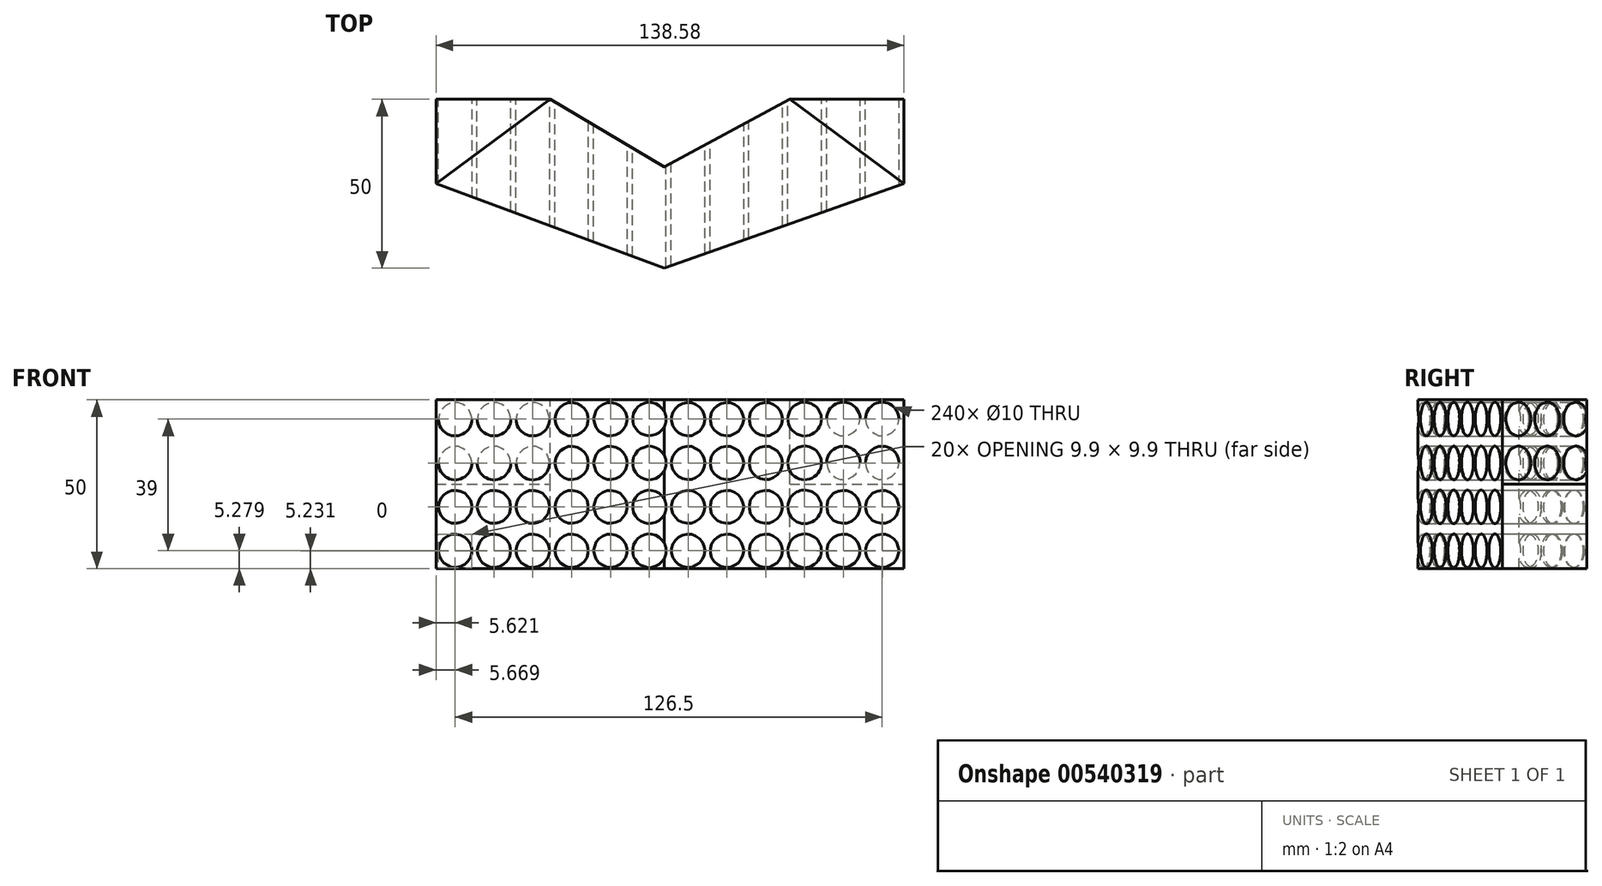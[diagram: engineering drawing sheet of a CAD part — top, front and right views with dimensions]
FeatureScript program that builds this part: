
annotation { "Feature Type Name" : "Feature", "Feature Type Description" : "" }
export const myFeature = defineFeature(function(context is Context, id is Id, definition is map)
    precondition{}
    {
        {
            var Q0;
            Q0=qCreatedBy(makeId("Front.planeOp"),FACE);
            var sketch = newSketch(context, id + "F0", { "sketchPlane" : qUnion([Q0])});
            skLineSegment(sketch, "E0.bottom", {"start": v(-67.58, 0) * mm, "end": v(71, 0) * mm});
            skLineSegment(sketch, "E0.top", {"start": v(-67.58, -50) * mm, "end": v(71, -50) * mm});
            skLineSegment(sketch, "E0.left", {"start": v(-67.58, 0) * mm, "end": v(-67.58, -50) * mm});
            skLineSegment(sketch, "E0.right", {"start": v(71, 0) * mm, "end": v(71, -50) * mm});
            skSolve(sketch);
        }
        {
            var Q0;
            Q0 = qSketchRegion(id + "F0", true);
            extrude(context, id + "F1", {"entities" : qUnion([Q0]), "depth" : 50 * mm, "offsetDistance" : 25 * mm});
        }
        {
            var Q0;
            Q0=makeQuery(id+"F0.imprint","IMPRINT",FACE,{"disambiguationData":[TD([[makeQuery(id+"F0.imprint","IMPRINT",EDGE,{"derivedFrom":sQuery(id+"F0.wireOp",EDGE,"E0.bottom")}),-1.0]])]});
            var sketch = newSketch(context, id + "F2", { "sketchPlane" : qUnion([Q0])});
            skCircle(sketch, "E1", {"center": v(-61.91, -5.72) * mm, "radius": 5 * mm});
            skCircle(sketch, "E2.0.1.0", {"center": v(-61.91, -18.72) * mm, "radius": 5 * mm});
            skCircle(sketch, "E2.0.2.0", {"center": v(-61.91, -31.72) * mm, "radius": 5 * mm});
            skCircle(sketch, "E2.0.3.0", {"center": v(-61.91, -44.72) * mm, "radius": 5 * mm});
            skCircle(sketch, "E2.1.0.0", {"center": v(-50.41, -5.72) * mm, "radius": 5 * mm});
            skCircle(sketch, "E2.1.1.0", {"center": v(-50.41, -18.72) * mm, "radius": 5 * mm});
            skCircle(sketch, "E2.1.2.0", {"center": v(-50.41, -31.72) * mm, "radius": 5 * mm});
            skCircle(sketch, "E2.1.3.0", {"center": v(-50.41, -44.72) * mm, "radius": 5 * mm});
            skCircle(sketch, "E2.2.0.0", {"center": v(-38.91, -5.72) * mm, "radius": 5 * mm});
            skCircle(sketch, "E2.2.1.0", {"center": v(-38.91, -18.72) * mm, "radius": 5 * mm});
            skCircle(sketch, "E2.2.2.0", {"center": v(-38.91, -31.72) * mm, "radius": 5 * mm});
            skCircle(sketch, "E2.2.3.0", {"center": v(-38.91, -44.72) * mm, "radius": 5 * mm});
            skCircle(sketch, "E2.3.0.0", {"center": v(-27.41, -5.72) * mm, "radius": 5 * mm});
            skCircle(sketch, "E2.3.1.0", {"center": v(-27.41, -18.72) * mm, "radius": 5 * mm});
            skCircle(sketch, "E2.3.2.0", {"center": v(-27.41, -31.72) * mm, "radius": 5 * mm});
            skCircle(sketch, "E2.3.3.0", {"center": v(-27.41, -44.72) * mm, "radius": 5 * mm});
            skCircle(sketch, "E2.4.0.0", {"center": v(-15.91, -5.72) * mm, "radius": 5 * mm});
            skCircle(sketch, "E2.4.1.0", {"center": v(-15.91, -18.72) * mm, "radius": 5 * mm});
            skCircle(sketch, "E2.4.2.0", {"center": v(-15.91, -31.72) * mm, "radius": 5 * mm});
            skCircle(sketch, "E2.4.3.0", {"center": v(-15.91, -44.72) * mm, "radius": 5 * mm});
            skCircle(sketch, "E2.5.0.0", {"center": v(-4.41, -5.72) * mm, "radius": 5 * mm});
            skCircle(sketch, "E2.5.1.0", {"center": v(-4.41, -18.72) * mm, "radius": 5 * mm});
            skCircle(sketch, "E2.5.2.0", {"center": v(-4.41, -31.72) * mm, "radius": 5 * mm});
            skCircle(sketch, "E2.5.3.0", {"center": v(-4.41, -44.72) * mm, "radius": 5 * mm});
            skCircle(sketch, "E2.6.0.0", {"center": v(7.09, -5.72) * mm, "radius": 5 * mm});
            skCircle(sketch, "E2.6.1.0", {"center": v(7.09, -18.72) * mm, "radius": 5 * mm});
            skCircle(sketch, "E2.6.2.0", {"center": v(7.09, -31.72) * mm, "radius": 5 * mm});
            skCircle(sketch, "E2.6.3.0", {"center": v(7.09, -44.72) * mm, "radius": 5 * mm});
            skCircle(sketch, "E2.7.0.0", {"center": v(18.59, -5.72) * mm, "radius": 5 * mm});
            skCircle(sketch, "E2.7.1.0", {"center": v(18.59, -18.72) * mm, "radius": 5 * mm});
            skCircle(sketch, "E2.7.2.0", {"center": v(18.59, -31.72) * mm, "radius": 5 * mm});
            skCircle(sketch, "E2.7.3.0", {"center": v(18.59, -44.72) * mm, "radius": 5 * mm});
            skCircle(sketch, "E2.8.0.0", {"center": v(30.09, -5.72) * mm, "radius": 5 * mm});
            skCircle(sketch, "E2.8.1.0", {"center": v(30.09, -18.72) * mm, "radius": 5 * mm});
            skCircle(sketch, "E2.8.2.0", {"center": v(30.09, -31.72) * mm, "radius": 5 * mm});
            skCircle(sketch, "E2.8.3.0", {"center": v(30.09, -44.72) * mm, "radius": 5 * mm});
            skCircle(sketch, "E2.9.0.0", {"center": v(41.59, -5.72) * mm, "radius": 5 * mm});
            skCircle(sketch, "E2.9.1.0", {"center": v(41.59, -18.72) * mm, "radius": 5 * mm});
            skCircle(sketch, "E2.9.2.0", {"center": v(41.59, -31.72) * mm, "radius": 5 * mm});
            skCircle(sketch, "E2.9.3.0", {"center": v(41.59, -44.72) * mm, "radius": 5 * mm});
            skCircle(sketch, "E2.10.0.0", {"center": v(53.09, -5.72) * mm, "radius": 5 * mm});
            skCircle(sketch, "E2.10.1.0", {"center": v(53.09, -18.72) * mm, "radius": 5 * mm});
            skCircle(sketch, "E2.10.2.0", {"center": v(53.09, -31.72) * mm, "radius": 5 * mm});
            skCircle(sketch, "E2.10.3.0", {"center": v(53.09, -44.72) * mm, "radius": 5 * mm});
            skCircle(sketch, "E2.11.0.0", {"center": v(64.59, -5.72) * mm, "radius": 5 * mm});
            skCircle(sketch, "E2.11.1.0", {"center": v(64.59, -18.72) * mm, "radius": 5 * mm});
            skCircle(sketch, "E2.11.2.0", {"center": v(64.59, -31.72) * mm, "radius": 5 * mm});
            skCircle(sketch, "E2.11.3.0", {"center": v(64.59, -44.72) * mm, "radius": 5 * mm});
            skLineSegment(sketch, "E2.direction1", {"start": v(-61.91, -5.72) * mm, "end": v(-50.41, -5.72) * mm, "construction": true});
            skLineSegment(sketch, "E2.direction2", {"start": v(-61.91, -5.72) * mm, "end": v(-61.91, -18.72) * mm, "construction": true});
            skSolve(sketch);
        }
        {
            var Q0;
            Q0 = qSketchRegion(id + "F2", true);
            extrude(context, id + "F3", {"entities" : qUnion([Q0]), "operationType" : NewBodyOperationType.REMOVE, "endBound" : BoundingType.THROUGH_ALL, "depth" : 20 * mm, "offsetDistance" : 25 * mm});
        }
        {
            var Q0;
            Q0=makeQuery(id+"F1.opExtrude","SWEPT_FACE",FACE,{"disambiguationData":[OSD([sQuery(id+"F0.wireOp",EDGE,"E0.bottom")])]});
            var sketch = newSketch(context, id + "F4", { "sketchPlane" : qUnion([Q0])});
            skPoint(sketch, "E3", {"position": v(-67.58, 0) * mm});
            skPoint(sketch, "E4", {"position": v(71, 0) * mm});
            skPoint(sketch, "E5", {"position": v(0, 0) * mm});
            skPoint(sketch, "E6", {"position": v(-33.79, 0) * mm});
            skPoint(sketch, "E7", {"position": v(37.2, 0) * mm});
            skPoint(sketch, "E8", {"position": v(0, -20) * mm});
            skLineSegment(sketch, "E9", {"start": v(-33.79, 0) * mm, "end": v(0, -20) * mm});
            skLineSegment(sketch, "E10", {"start": v(37.2, 0) * mm, "end": v(0, -20) * mm});
            skLineSegment(sketch, "E11", {"start": v(-33.79, 0) * mm, "end": v(37.2, 0) * mm});
            skSolve(sketch);
        }
        {
            var Q0;
            Q0 = qSketchRegion(id + "F4", true);
            extrude(context, id + "F5", {"entities" : qUnion([Q0]), "operationType" : NewBodyOperationType.REMOVE, "endBound" : BoundingType.THROUGH_ALL, "oppositeDirection" : true, "depth" : 25 * mm, "offsetDistance" : 25 * mm});
        }
        {
            var Q0;
            Q0=makeQuery(id+"F1.opExtrude","SWEPT_FACE",FACE,{"disambiguationData":[OSD([sQuery(id+"F0.wireOp",EDGE,"E0.bottom")])]});
            var sketch = newSketch(context, id + "F6", { "sketchPlane" : qUnion([Q0])});
            skPoint(sketch, "E12", {"position": v(-67.58, 0) * mm});
            skPoint(sketch, "E13", {"position": v(-67.58, -50) * mm});
            skPoint(sketch, "E14", {"position": v(71, -25) * mm});
            skLineSegment(sketch, "E15", {"start": v(-67.58, -25) * mm, "end": v(0, -50) * mm});
            skLineSegment(sketch, "E16", {"start": v(0, -50) * mm, "end": v(71, -25) * mm});
            skLineSegment(sketch, "E17", {"start": v(-67.58, -25) * mm, "end": v(-67.58, -50) * mm});
            skLineSegment(sketch, "E18", {"start": v(0, -50) * mm, "end": v(-67.58, -50) * mm});
            skLineSegment(sketch, "E19", {"start": v(71, -50) * mm, "end": v(71, -25) * mm});
            skSolve(sketch);
        }
        {
            var Q0;
            Q0=makeQuery(id+"F6.imprint","IMPRINT",FACE,{"disambiguationData":[TD([[makeQuery(id+"F6.imprint","IMPRINT",EDGE,{"derivedFrom":sQuery(id+"F6.wireOp",EDGE,"E15")}),-1.0]])]});
            var Q1;
            {var subQ0=sQuery(id+"F6.wireOp",EDGE,"E16");Q1=makeQuery(id+"F6.imprint","IMPRINT",FACE,{"disambiguationData":[TD([[makeQuery(id+"F6.imprint","IMPRINT",EDGE,{"derivedFrom":subQ0}),-1.0]])]});}
            extrude(context, id + "F7", {"entities" : qUnion([Q0, Q1]), "operationType" : NewBodyOperationType.REMOVE, "endBound" : BoundingType.THROUGH_ALL, "oppositeDirection" : true, "depth" : 25 * mm, "offsetDistance" : 25 * mm});
        }
        {
            var Q0;
            Q0=makeQuery(id+"F1.opExtrude","SWEPT_FACE",FACE,{"disambiguationData":[OSD([sQuery(id+"F0.wireOp",EDGE,"E0.bottom")])]});
            var sketch = newSketch(context, id + "F8", { "sketchPlane" : qUnion([Q0])});
            skLineSegment(sketch, "E20", {"start": v(-67.58, -25) * mm, "end": v(-33.79, 0) * mm});
            skLineSegment(sketch, "E21", {"start": v(-33.79, 0) * mm, "end": v(-67.58, 0) * mm});
            skLineSegment(sketch, "E22", {"start": v(-67.58, 0) * mm, "end": v(-67.58, -25) * mm});
            skLineSegment(sketch, "E23", {"start": v(37.2, 0) * mm, "end": v(71, -25) * mm});
            skLineSegment(sketch, "E24", {"start": v(71, -25) * mm, "end": v(71, 0) * mm});
            skLineSegment(sketch, "E25", {"start": v(71, 0) * mm, "end": v(39.78, 0) * mm});
            skSolve(sketch);
        }
        {
            var Q0;
            Q0=makeQuery(id+"F8.imprint","IMPRINT",FACE,{"disambiguationData":[TD([[makeQuery(id+"F8.imprint","IMPRINT",EDGE,{"derivedFrom":sQuery(id+"F8.wireOp",EDGE,"E20")}),1.0]])]});
            var Q1;
            {var subQ0=sQuery(id+"F8.wireOp",EDGE,"E23");Q1=makeQuery(id+"F8.imprint","IMPRINT",FACE,{"disambiguationData":[TD([[makeQuery(id+"F8.imprint","IMPRINT",EDGE,{"derivedFrom":subQ0}),1.0]])]});}
            extrude(context, id + "F9", {"entities" : qUnion([Q0, Q1]), "operationType" : NewBodyOperationType.REMOVE, "oppositeDirection" : true, "depth" : 25 * mm, "offsetDistance" : 25 * mm});
        }
    });
